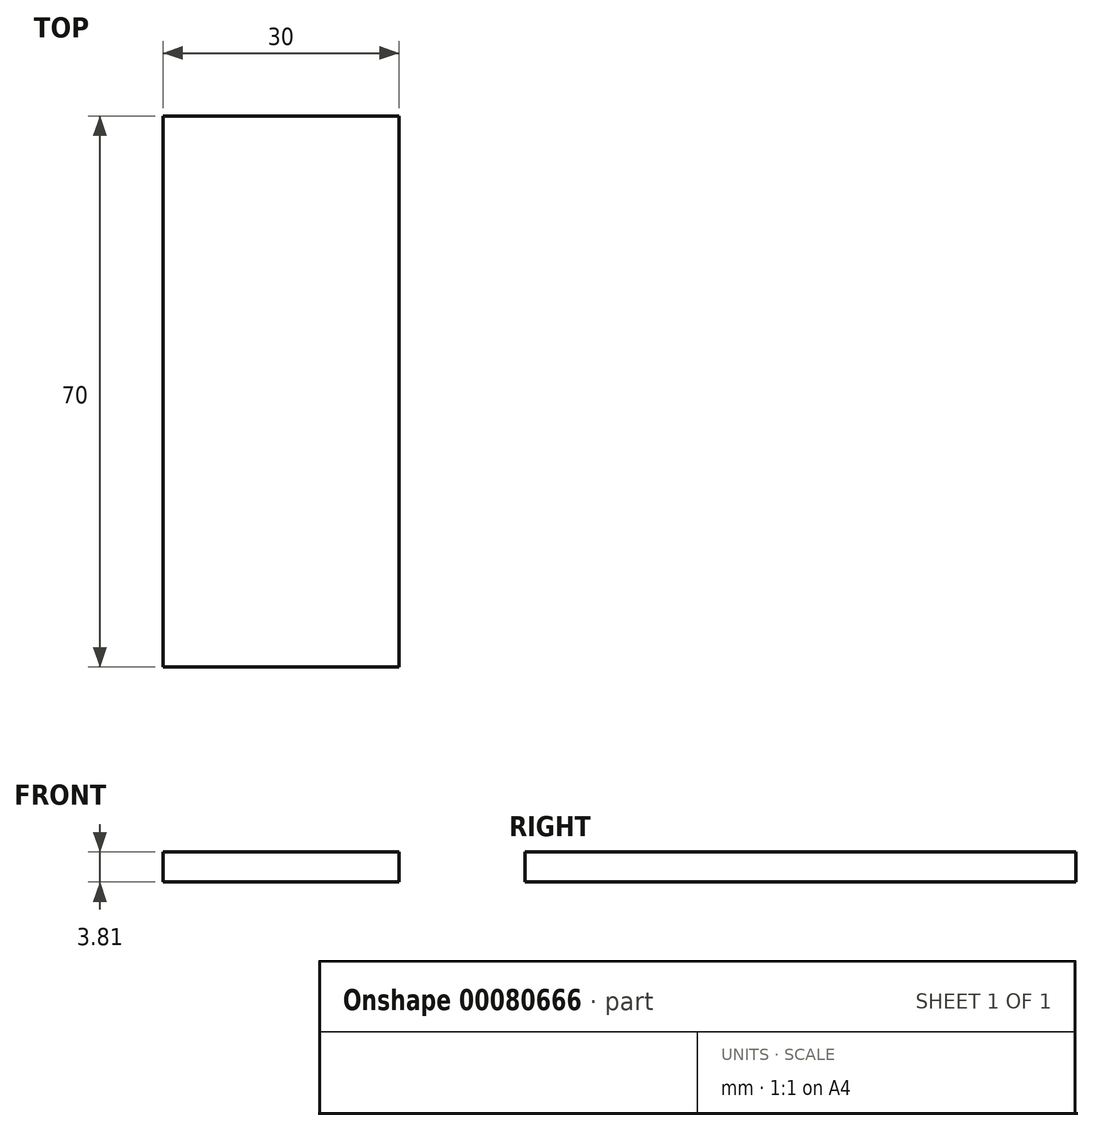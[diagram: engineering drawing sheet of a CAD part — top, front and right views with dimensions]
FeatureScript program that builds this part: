
annotation { "Feature Type Name" : "Feature", "Feature Type Description" : "" }
export const myFeature = defineFeature(function(context is Context, id is Id, definition is map)
    precondition{}
    {
        {
            var Q0;
            Q0=qCreatedBy(makeId("Top.planeOp"),FACE);
            var sketch = newSketch(context, id + "F0", { "sketchPlane" : qUnion([Q0])});
            skLineSegment(sketch, "E0.bottom", {"start": v(15, -35) * mm, "end": v(-15, -35) * mm});
            skLineSegment(sketch, "E0.top", {"start": v(15, 35) * mm, "end": v(-15, 35) * mm});
            skLineSegment(sketch, "E0.left", {"start": v(15, -35) * mm, "end": v(15, 35) * mm});
            skLineSegment(sketch, "E0.right", {"start": v(-15, -35) * mm, "end": v(-15, 35) * mm});
            skPoint(sketch, "E0.middle", {"position": v(0, 0) * mm});
            skSolve(sketch);
        }
        {
            var Q0;
            Q0 = qSketchRegion(id + "F0", true);
            extrude(context, id + "F1", {"entities" : qUnion([Q0]), "depth" : 3.81 * mm});
        }
    });
